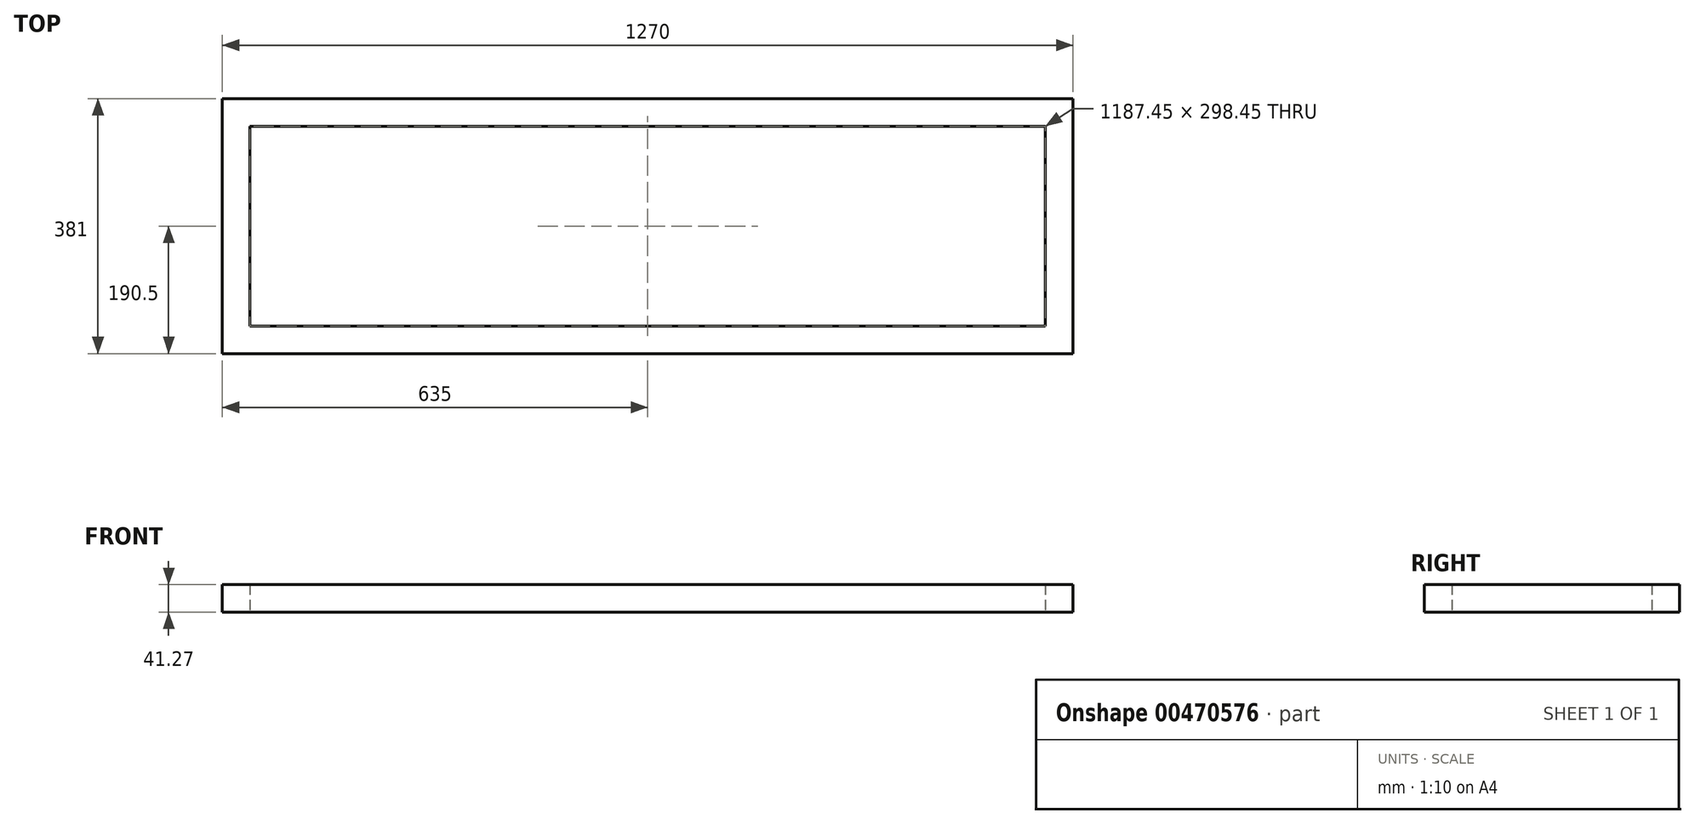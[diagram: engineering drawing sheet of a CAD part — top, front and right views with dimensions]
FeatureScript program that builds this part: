
annotation { "Feature Type Name" : "Feature", "Feature Type Description" : "" }
export const myFeature = defineFeature(function(context is Context, id is Id, definition is map)
    precondition{}
    {
        {
            var Q0;
            Q0=qCreatedBy(makeId("Top.planeOp"),FACE);
            var sketch = newSketch(context, id + "F0", { "sketchPlane" : qUnion([Q0])});
            skLineSegment(sketch, "E0.bottom", {"start": v(635, -190.5) * mm, "end": v(-635, -190.5) * mm});
            skLineSegment(sketch, "E0.top", {"start": v(635, 190.5) * mm, "end": v(-635, 190.5) * mm});
            skLineSegment(sketch, "E0.left", {"start": v(635, -190.5) * mm, "end": v(635, 190.5) * mm});
            skLineSegment(sketch, "E0.right", {"start": v(-635, -190.5) * mm, "end": v(-635, 190.5) * mm});
            skPoint(sketch, "E0.middle", {"position": v(0, 0) * mm});
            skLineSegment(sketch, "E1.bottom", {"start": v(593.73, -149.22) * mm, "end": v(-593.72, -149.23) * mm});
            skLineSegment(sketch, "E1.top", {"start": v(593.72, 149.23) * mm, "end": v(-593.73, 149.22) * mm});
            skLineSegment(sketch, "E1.left", {"start": v(593.72, -149.22) * mm, "end": v(593.72, 149.23) * mm});
            skLineSegment(sketch, "E1.right", {"start": v(-593.73, -149.23) * mm, "end": v(-593.73, 149.22) * mm});
            skSolve(sketch);
        }
        {
            var Q0;
            Q0 = qSketchRegion(id + "F0", true);
            extrude(context, id + "F1", {"entities" : qUnion([Q0]), "depth" : 41.27 * mm});
        }
    });
